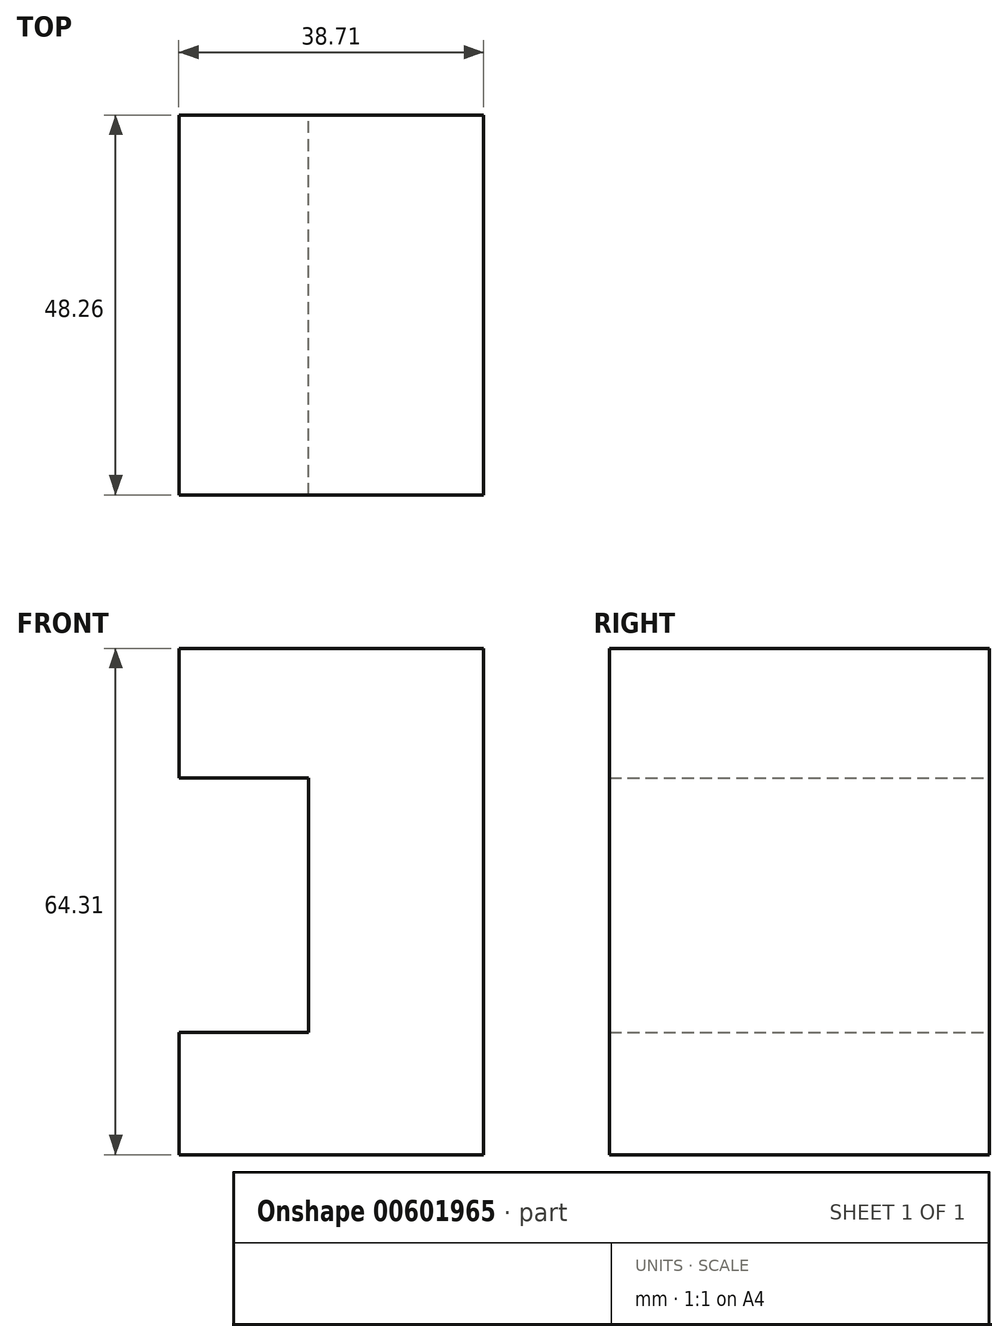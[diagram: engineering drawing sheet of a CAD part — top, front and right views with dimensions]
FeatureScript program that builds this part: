
annotation { "Feature Type Name" : "Feature", "Feature Type Description" : "" }
export const myFeature = defineFeature(function(context is Context, id is Id, definition is map)
    precondition{}
    {
        {
            var Q0;
            Q0=qCreatedBy(makeId("Front.planeOp"),FACE);
            var sketch = newSketch(context, id + "F0", { "sketchPlane" : qUnion([Q0])});
            skLineSegment(sketch, "E0", {"start": v(-33.99, 32) * mm, "end": v(-33.99, 15.54) * mm});
            skLineSegment(sketch, "E1", {"start": v(-33.99, 15.54) * mm, "end": v(-17.53, 15.54) * mm});
            skLineSegment(sketch, "E2", {"start": v(-17.53, 15.54) * mm, "end": v(-17.53, -16.76) * mm});
            skLineSegment(sketch, "E3", {"start": v(-17.53, -16.76) * mm, "end": v(-33.99, -16.76) * mm});
            skLineSegment(sketch, "E4", {"start": v(-33.99, -16.76) * mm, "end": v(-33.99, -32.3) * mm});
            skLineSegment(sketch, "E5", {"start": v(-33.99, -32.3) * mm, "end": v(4.72, -32.3) * mm});
            skLineSegment(sketch, "E6", {"start": v(4.72, -32.3) * mm, "end": v(4.72, 32) * mm});
            skLineSegment(sketch, "E7", {"start": v(4.72, 32) * mm, "end": v(-33.99, 32) * mm});
            skSolve(sketch);
        }
        {
            var Q0;
            Q0=makeQuery(id+"F0.imprint","IMPRINT",FACE,{"disambiguationData":[TD([[makeQuery(id+"F0.imprint","IMPRINT",EDGE,{"derivedFrom":sQuery(id+"F0.wireOp",EDGE,"E0")}),1.0]])]});
            extrude(context, id + "F1", {"entities" : qUnion([Q0]), "depth" : 48.26 * mm, "offsetDistance" : 25.4 * mm});
        }
    });
